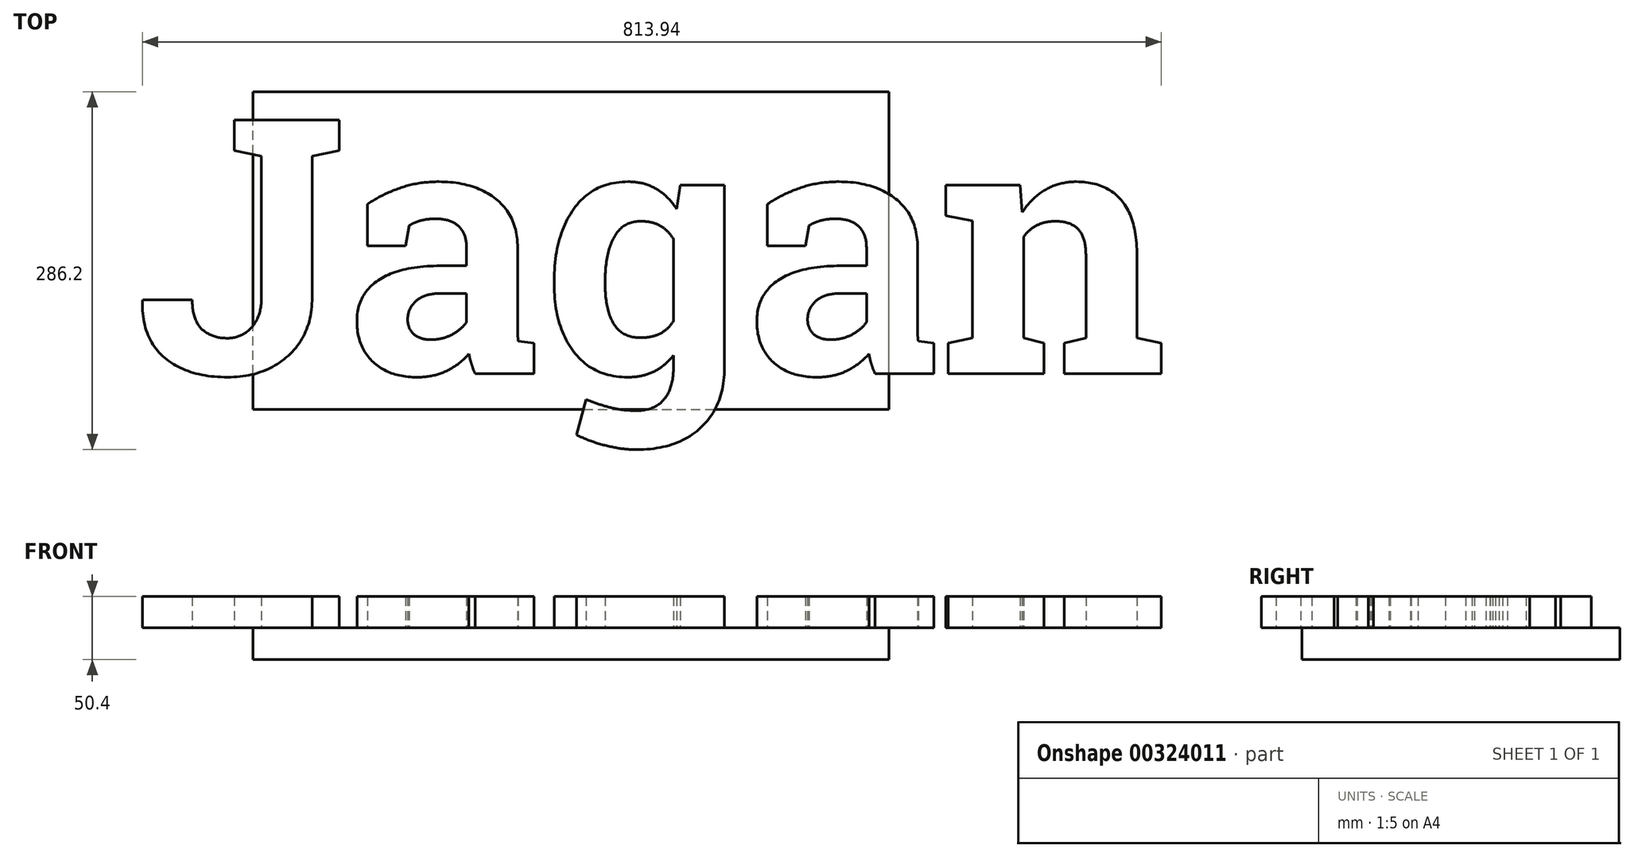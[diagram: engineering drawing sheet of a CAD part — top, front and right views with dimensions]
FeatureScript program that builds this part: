
annotation { "Feature Type Name" : "Feature", "Feature Type Description" : "" }
export const myFeature = defineFeature(function(context is Context, id is Id, definition is map)
    precondition{}
    {
        {
            var Q0;
            Q0=qCreatedBy(makeId("Top.planeOp"),FACE);
            var sketch = newSketch(context, id + "F0", { "sketchPlane" : qUnion([Q0])});
            skLineSegment(sketch, "E0.bottom", {"start": v(-207.81, -127.78) * mm, "end": v(300.19, -127.78) * mm});
            skLineSegment(sketch, "E0.top", {"start": v(-207.81, 126.22) * mm, "end": v(300.19, 126.22) * mm});
            skLineSegment(sketch, "E0.left", {"start": v(-207.81, -127.78) * mm, "end": v(-207.81, 126.22) * mm});
            skLineSegment(sketch, "E0.right", {"start": v(300.19, -127.78) * mm, "end": v(300.19, 126.22) * mm});
            skLineSegment(sketch, "E1", {"start": v(-207.81, -127.78) * mm, "end": v(300.19, 126.22) * mm});
            skLineSegment(sketch, "E2", {"start": v(-207.81, 126.22) * mm, "end": v(300.19, -127.78) * mm});
            skSolve(sketch);
        }
        {
            var Q0;
            Q0 = qSketchRegion(id + "F0", true);
            extrude(context, id + "F1", {"entities" : qUnion([Q0]), "depth" : 25.4 * mm});
        }
        {
            var Q0;
            Q0=makeQuery(id+"F1.opExtrude","CAP_FACE",FACE,{"disambiguationData":[OSD([sQuery(id+"F0.wireOp",EDGE,"E0.bottom"),sQuery(id+"F0.wireOp",EDGE,"E0.top"),sQuery(id+"F0.wireOp",EDGE,"E0.left"),sQuery(id+"F0.wireOp",EDGE,"E0.right")])],"isStart":false});
            var sketch = newSketch(context, id + "F2", { "sketchPlane" : qUnion([Q0])});
            skText(sketch, "E3", { "text": "Jagan", "fontName": "RobotoSlab-Bold.ttf"});
            const initialGuessF2  = {"E3": [-0.30085, -0.09914, 1, 0, 0.20525]};
            skSetInitialGuess(sketch, initialGuessF2);
            skSolve(sketch);
        }
        {
            var Q0;
            Q0 = qSketchRegion(id + "F2", true);
            extrude(context, id + "F3", {"entities" : qUnion([Q0]), "operationType" : NewBodyOperationType.ADD, "depth" : 25 * mm});
        }
    });
